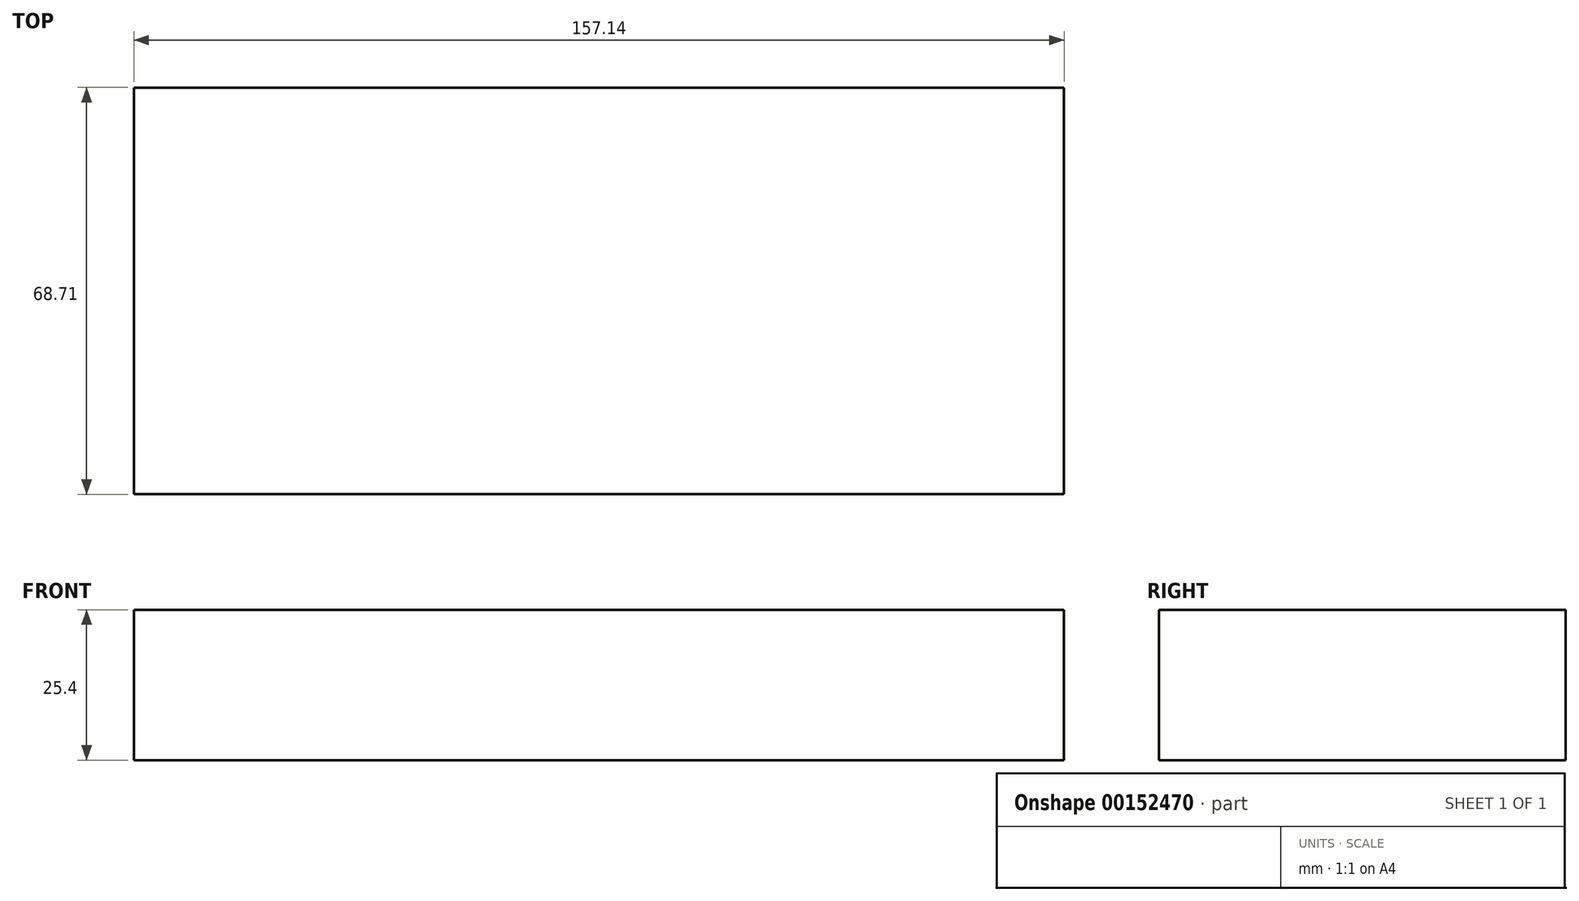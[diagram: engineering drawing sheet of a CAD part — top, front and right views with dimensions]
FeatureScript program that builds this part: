
annotation { "Feature Type Name" : "Feature", "Feature Type Description" : "" }
export const myFeature = defineFeature(function(context is Context, id is Id, definition is map)
    precondition{}
    {
        {
            var Q0;
            Q0=qCreatedBy(makeId("Top.planeOp"),FACE);
            var sketch = newSketch(context, id + "F0", { "sketchPlane" : qUnion([Q0])});
            skLineSegment(sketch, "E0.bottom", {"start": v(-77.7, 28.8) * mm, "end": v(79.45, 28.8) * mm});
            skLineSegment(sketch, "E0.top", {"start": v(-77.7, -39.9) * mm, "end": v(79.45, -39.9) * mm});
            skLineSegment(sketch, "E0.left", {"start": v(-77.7, 28.8) * mm, "end": v(-77.7, -39.9) * mm});
            skLineSegment(sketch, "E0.right", {"start": v(79.45, 28.8) * mm, "end": v(79.45, -39.9) * mm});
            skSolve(sketch);
        }
        {
            var Q0;
            Q0 = qSketchRegion(id + "F0", true);
            extrude(context, id + "F1", {"entities" : qUnion([Q0]), "depth" : 25.4 * mm});
        }
    });
